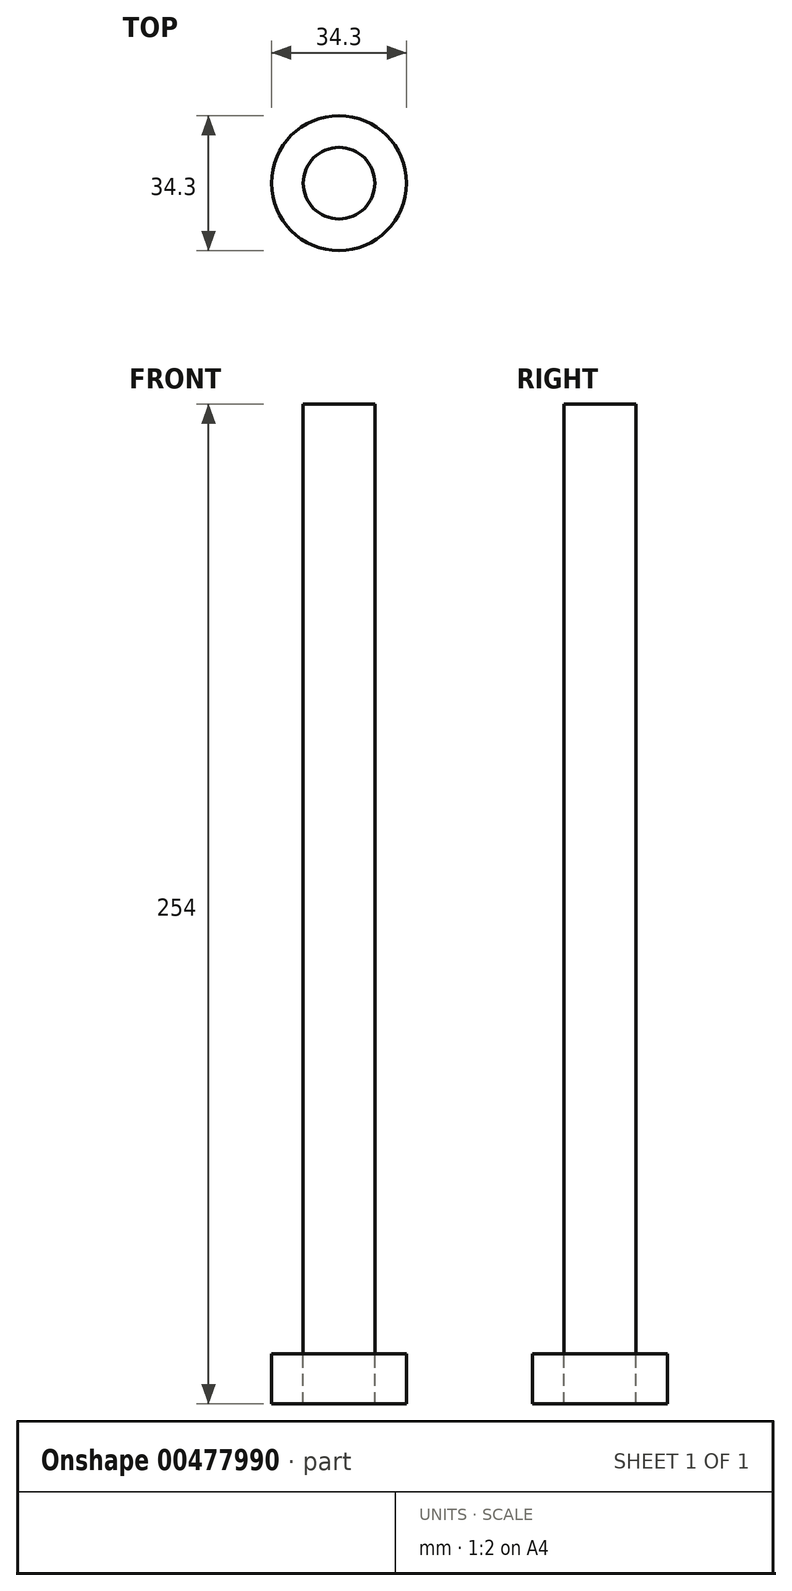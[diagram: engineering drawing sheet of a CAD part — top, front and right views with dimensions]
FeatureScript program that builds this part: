
annotation { "Feature Type Name" : "Feature", "Feature Type Description" : "" }
export const myFeature = defineFeature(function(context is Context, id is Id, definition is map)
    precondition{}
    {
        {
            var Q0;
            Q0=qCreatedBy(makeId("Top.planeOp"),FACE);
            var sketch = newSketch(context, id + "F0", { "sketchPlane" : qUnion([Q0])});
            skCircle(sketch, "E0", {"center": v(0, 0) * mm, "radius": 9.1 * mm});
            skSolve(sketch);
        }
        {
            var Q0;
            Q0=sQuery(id+"F0.wireOp",EDGE,"E0");
            extrude(context, id + "F1", {"bodyType" : ToolBodyType.SURFACE, "surfaceEntities" : qUnion([Q0]), "depth" : 254 * mm});
        }
        {
            var Q0;
            Q0=qCreatedBy(makeId("Top.planeOp"),FACE);
            var sketch = newSketch(context, id + "F2", { "sketchPlane" : qUnion([Q0])});
            skCircle(sketch, "E1", {"center": v(0, 0) * mm, "radius": 6.87 * mm});
            skCircle(sketch, "E2", {"center": v(0, 0) * mm, "radius": 17.15 * mm});
            skSolve(sketch);
        }
        {
            var Q0;
            Q0=sQuery(id+"F2.wireOp",EDGE,"E2");
            extrude(context, id + "F3", {"bodyType" : ToolBodyType.SURFACE, "surfaceEntities" : qUnion([Q0]), "depth" : 12.7 * mm});
        }
    });
